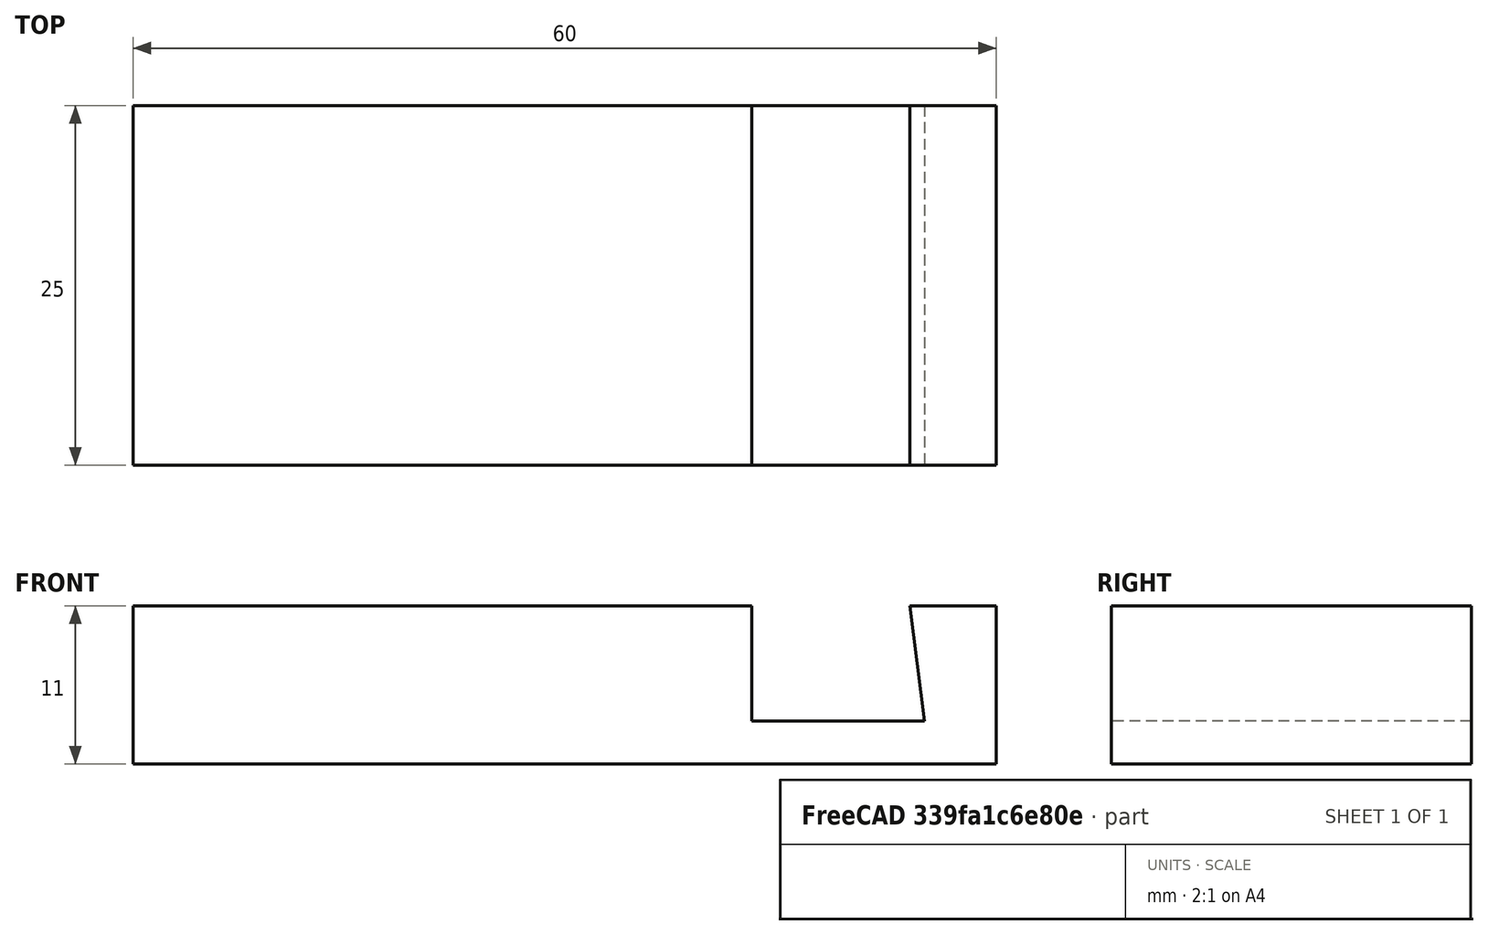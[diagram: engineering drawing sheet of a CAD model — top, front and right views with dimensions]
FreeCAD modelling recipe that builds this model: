
FCSTD DOCUMENT  (FreeCAD 1.0R38806 (Git))
Label: soporte_movil
License: All rights reserved
LicenseURL: https://en.wikipedia.org/wiki/All_rights_reserved
objects: Sketcher::SketchObject×1, Part::Extrusion×1
note: 3 computed .brp shape members not serialized (recipe doc carries the construction recipe); baked Part::Feature solids carry a one-line shape summary decoded from their .brp

FEATURE [Sketcher::SketchObject] Sketch
  ArcFitTolerance = 1e-06
  FullyConstrained = false
  MakeInternals = false
  sketch-geometry (8):
    g0: LineSegment StartX=0 StartY=11 StartZ=0 EndX=0 EndY=0 EndZ=0
    g1: LineSegment StartX=0 StartY=0 StartZ=0 EndX=60 EndY=0 EndZ=0
    g2: LineSegment StartX=60 StartY=0 StartZ=0 EndX=60 EndY=11 EndZ=0
    g3: LineSegment StartX=60 StartY=11 StartZ=0 EndX=54 EndY=11 EndZ=0
    g4: LineSegment StartX=54 StartY=11 StartZ=0 EndX=55 EndY=3 EndZ=0
    g5: LineSegment StartX=55 StartY=3 StartZ=0 EndX=43 EndY=3 EndZ=0
    g6: LineSegment StartX=43 StartY=3 StartZ=0 EndX=43 EndY=11 EndZ=0
    g7: LineSegment StartX=43 StartY=11 StartZ=0 EndX=0 EndY=11 EndZ=0
  constraints (22):
    c: PointOnObject(g0,g-2)
    c: Coincident(g0,g-1)
    c: Coincident(g0,g1)
    c: PointOnObject(g1,g-1)
    c: Coincident(g1,g2)
    c: Vertical(g2)
    c: Coincident(g2,g3)
    c: Horizontal(g3)
    c: Coincident(g3,g4)
    c: Coincident(g4,g5)
    c: Horizontal(g5)
    c: Coincident(g5,g6)
    c: Vertical(g6)
    c: Coincident(g6,g7)
    c: Coincident(g7,g0)
    c: Horizontal(g7)
    c: Distance(g0,g0) = 11
    c: DistanceX(g1,g1) = 60
    c: Distance(g3,g3) = 6
    c: DistanceY(g-1,g4) = 3
    c: DistanceX(g5,g4) = 12
    c: DistanceX(g6,g3) = 11
FEATURE [Part::Extrusion] Extrude
  Base = -> Sketch
  Dir = (0,0,1)
  DirMode = 0
  FaceMakerClass = Part::FaceMakerBullseye
  FaceMakerMode = 3
  LengthFwd = 25
  LengthRev = 0
  Placement = pos=(0,0,0) rot=(1,0,0;1.5708rad)
  Solid = true
  Symmetric = false
